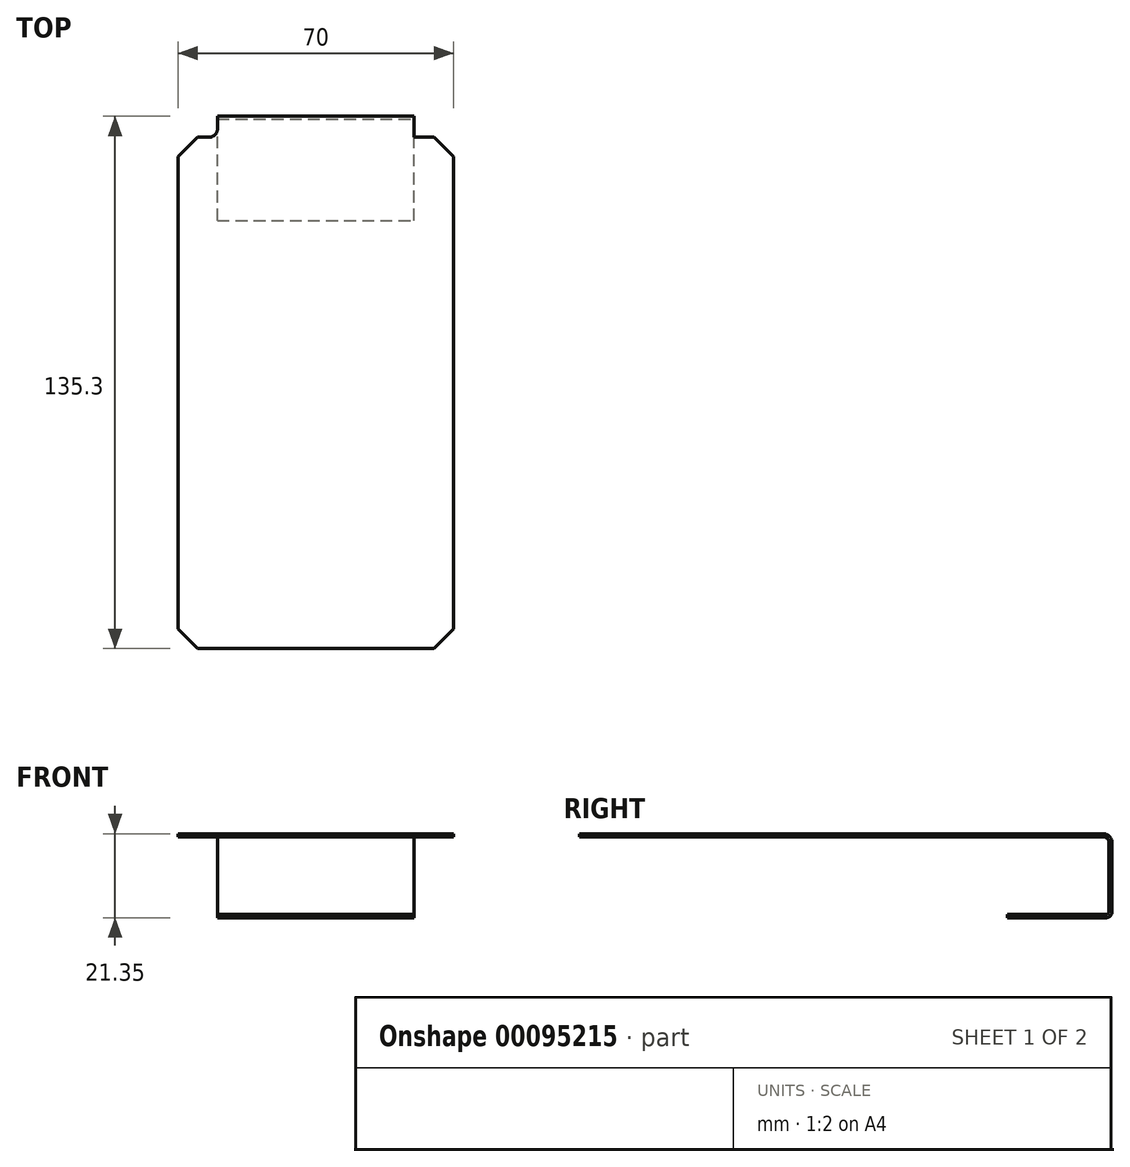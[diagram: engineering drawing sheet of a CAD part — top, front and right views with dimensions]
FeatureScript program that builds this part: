
annotation { "Feature Type Name" : "Feature", "Feature Type Description" : "" }
export const myFeature = defineFeature(function(context is Context, id is Id, definition is map)
    precondition{}
    {
        {
            var Q0;
            Q0=qCreatedBy(makeId("Top.planeOp"),FACE);
            var sketch = newSketch(context, id + "F0", { "sketchPlane" : qUnion([Q0])});
            skLineSegment(sketch, "E0.bottom", {"start": v(-40.7, 26.6) * mm, "end": v(29.3, 26.6) * mm});
            skLineSegment(sketch, "E0.top", {"start": v(-40.7, -103.4) * mm, "end": v(29.3, -103.4) * mm});
            skLineSegment(sketch, "E0.left", {"start": v(-40.7, 26.6) * mm, "end": v(-40.7, -103.4) * mm});
            skLineSegment(sketch, "E0.right", {"start": v(29.3, 26.6) * mm, "end": v(29.3, -103.4) * mm});
            skSolve(sketch);
        }
        {
            var Q0;
            Q0 = qSketchRegion(id + "F0", true);
            extrude(context, id + "F1", {"entities" : qUnion([Q0]), "depth" : 0.8 * mm});
        }
        {
            var Q0;
            Q0=makeQuery(id+"F1.opExtrude","SWEPT_EDGE",EDGE,{"disambiguationData":[OSD([sQuery(id+"F0.wireOp",EDGE,"E0.top"),sQuery(id+"F0.wireOp",EDGE,"E0.left")])]});
            var Q1;
            Q1=makeQuery(id+"F1.opExtrude","SWEPT_EDGE",EDGE,{"disambiguationData":[OSD([sQuery(id+"F0.wireOp",EDGE,"E0.top"),sQuery(id+"F0.wireOp",EDGE,"E0.right")])]});
            var Q2;
            Q2=makeQuery(id+"F1.opExtrude","SWEPT_EDGE",EDGE,{"disambiguationData":[OSD([sQuery(id+"F0.wireOp",EDGE,"E0.bottom"),sQuery(id+"F0.wireOp",EDGE,"E0.right")])]});
            var Q3;
            Q3=makeQuery(id+"F1.opExtrude","SWEPT_EDGE",EDGE,{"disambiguationData":[OSD([sQuery(id+"F0.wireOp",EDGE,"E0.bottom"),sQuery(id+"F0.wireOp",EDGE,"E0.left")])]});
            chamfer(context, id + "F2", {"entities" : qUnion([Q0, Q1, Q2, Q3]), "width" : 5 * mm, "tangentPropagation" : true});
        }
        {
            var Q0;
            Q0=makeQuery(id+"F1.opExtrude","SWEPT_FACE",FACE,{"disambiguationData":[OSD([sQuery(id+"F0.wireOp",EDGE,"E0.bottom")])]});
            var sketch = newSketch(context, id + "F3", { "sketchPlane" : qUnion([Q0])});
            skLineSegment(sketch, "E1.0", {"start": v(30.7, 0.8) * mm, "end": v(-19.3, 0.8) * mm});
            skLineSegment(sketch, "E1.1", {"start": v(30.7, 0) * mm, "end": v(-19.3, 0) * mm});
            skLineSegment(sketch, "E2", {"start": v(-19.3, 0.8) * mm, "end": v(-19.3, 0) * mm});
            skLineSegment(sketch, "E3", {"start": v(30.7, 0.8) * mm, "end": v(30.7, 0) * mm});
            skPoint(sketch, "E4.orphan", {"position": v(35.7, 0.8) * mm});
            skPoint(sketch, "E5.orphan", {"position": v(35.7, 0) * mm});
            skPoint(sketch, "E6.orphan", {"position": v(-24.3, 0.8) * mm});
            skPoint(sketch, "E7.orphan", {"position": v(-24.3, 0) * mm});
            skSolve(sketch);
        }
        {
            var Q0;
            Q0 = qSketchRegion(id + "F3", true);
            extrude(context, id + "F4", {"entities" : qUnion([Q0]), "operationType" : NewBodyOperationType.ADD, "depth" : 3 * mm});
        }
        {
            var Q0;
            Q0=makeQuery(id+"F4.opExtrude","CAP_FACE",FACE,{"disambiguationData":[OSD([sQuery(id+"F3.wireOp",EDGE,"E1.0"),sQuery(id+"F3.wireOp",EDGE,"E1.1"),sQuery(id+"F3.wireOp",EDGE,"E2"),sQuery(id+"F3.wireOp",EDGE,"E3")])],"isStart":false});
            var sketch = newSketch(context, id + "F5", { "sketchPlane" : qUnion([Q0])});
            skLineSegment(sketch, "E8", {"start": v(-25.32, -1.5) * mm, "end": v(39.36, -1.5) * mm, "construction": true});
            skSolve(sketch);
        }
        {
            var Q0;
            Q0=makeQuery(id+"F5.imprint","IMPRINT",FACE,{"disambiguationData":[TD([[makeQuery(id+"F5.imprint","IMPRINT",EDGE,{"derivedFrom":makeQuery(id+"F4.opExtrude","CAP_EDGE",EDGE,{"disambiguationData":[OSD([sQuery(id+"F3.wireOp",EDGE,"E1.0")])],"isStart":false})}),1.0]])]});
            var Q1;
            Q1=sQuery(id+"F5.wireOp",EDGE,"E8");
            revolve(context, id + "F6", {"operationType" : NewBodyOperationType.ADD, "entities" : qUnion([Q0]), "axis" : qUnion([Q1]), "revolveType" : RevolveType.ONE_DIRECTION, "angle" : 90 * degree});
        }
        {
            var Q0;
            Q0=makeQuery(id+"F6.opRevolve","CAP_FACE",FACE,{"disambiguationData":[OSD([sQuery(id+"F3.wireOp",EDGE,"E1.0"),sQuery(id+"F3.wireOp",EDGE,"E1.1"),sQuery(id+"F3.wireOp",EDGE,"E2"),sQuery(id+"F3.wireOp",EDGE,"E3")])],"isStart":false});
            extrude(context, id + "F7", {"entities" : qUnion([Q0]), "operationType" : NewBodyOperationType.ADD, "depth" : 17.5 * mm});
        }
        {
            var Q0;
            Q0=makeQuery(id+"F7.opExtrude","CAP_FACE",FACE,{"disambiguationData":[OSD([sQuery(id+"F3.wireOp",EDGE,"E1.0"),sQuery(id+"F3.wireOp",EDGE,"E1.1"),sQuery(id+"F3.wireOp",EDGE,"E2"),sQuery(id+"F3.wireOp",EDGE,"E3")])],"isStart":false});
            var sketch = newSketch(context, id + "F8", { "sketchPlane" : qUnion([Q0])});
            skLineSegment(sketch, "E9", {"start": v(-17.36, -30.34) * mm, "end": v(6.03, -30.34) * mm, "construction": true});
            skSolve(sketch);
        }
        {
            var Q0;
            Q0=makeQuery(id+"F8.imprint","IMPRINT",FACE,{"disambiguationData":[TD([[makeQuery(id+"F8.imprint","IMPRINT",EDGE,{"derivedFrom":makeQuery(id+"F7.opExtrude","CAP_EDGE",EDGE,{"disambiguationData":[OSD([sQuery(id+"F3.wireOp",EDGE,"E1.0")])],"isStart":false})}),1.0]])]});
            var Q1;
            Q1=sQuery(id+"F8.wireOp",EDGE,"E9");
            revolve(context, id + "F9", {"operationType" : NewBodyOperationType.ADD, "entities" : qUnion([Q0]), "axis" : qUnion([Q1]), "revolveType" : RevolveType.ONE_DIRECTION, "oppositeDirection" : true, "angle" : 90 * degree});
        }
        {
            var Q0;
            Q0=makeQuery(id+"F9.opRevolve","CAP_FACE",FACE,{"disambiguationData":[OSD([sQuery(id+"F3.wireOp",EDGE,"E1.0"),sQuery(id+"F3.wireOp",EDGE,"E1.1"),sQuery(id+"F3.wireOp",EDGE,"E2"),sQuery(id+"F3.wireOp",EDGE,"E3")])],"isStart":false});
            extrude(context, id + "F10", {"entities" : qUnion([Q0]), "operationType" : NewBodyOperationType.ADD, "depth" : 25 * mm});
        }
        {
            var Q0;
            Q0=makeQuery(id+"F4.opExtrude","CAP_EDGE",EDGE,{"disambiguationData":[OSD([sQuery(id+"F3.wireOp",EDGE,"E3")])],"isStart":true});
            var Q1;
            Q1=makeQuery(id+"F4.opExtrude","CAP_EDGE",EDGE,{"disambiguationData":[OSD([sQuery(id+"F3.wireOp",EDGE,"E2")])],"isStart":true});
            fillet(context, id + "F11", {"entities" : qUnion([Q0, Q1]), "radius" : 2 * mm, "tangentPropagation" : true, "allowEdgeOverflow" : false});
        }
    });
